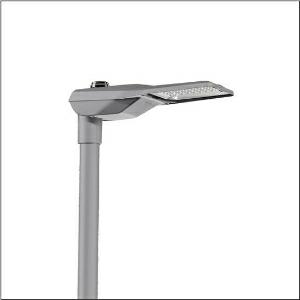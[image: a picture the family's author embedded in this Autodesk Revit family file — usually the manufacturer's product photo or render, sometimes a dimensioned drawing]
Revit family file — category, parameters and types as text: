
# Revit family: streetlight_sl_21_mini___st0_5a_5xe6b37n08gb_187f
name_source: partatom
category: Lighting Fixtures
units: mm (PartAtom-declared; Revit-internal decimal feet)

## family parameters
Cut with Voids When Loaded = No
Host = Face
Light Source = No
Part Type = Normal
Room Calculation Point = No
Round Connector Dimension = Use Diameter
Shared = No

## types (1)
- --- (1 x LED, 5940 lm, 40.4 W, 3000K)
    Apparent Load = 40 VA
    CIE Flux Codes = 41 75 97 100 100
    Color Rendering = 70
    Color Temperature = 3000K
    Default Elevation = 1800 mm
    Description = Streetlight SL 21 mini, mast luminaire, primary light control with lens, of PMMA, primary optical cover: cover, of toughened safety glass, transparent, light distribution: ST0.5a, light emission: direct distribution, primary light characteristic: asymmetric, installation type: side-entry, LED, 3G 1.5mm², High Power LED, rated luminous flux: 5.940lm, luminous efficacy: 147lm/W, light colour: 730, colour temperature: 3000K, control gear: NEMA (7pin), control: overheat protection, pre-setting: linear dimming characteristic, constant luminous flux control, time-dependent luminous flux control, flexible luminous flux parameterisation, mains connection: 230..240V, AC, 50/60Hz, connection cable pre-assembled, cable length: 8,5m, wiring characteristics: H07RN-F, start of lifetime: 40W, end of service life: 41W, reduction: 19W, luminaire housing, of diecast aluminium (EN AC-44300), powder-coated, Siteco® metallic grey (DB 702S), corrosivity category C5 mid according to DIN EN ISO 12944, multi-level sealing system, sealing non-destructively replaceable, inclination adjustable: 0°, 5°, 10°, 15°, length: 628mm, width: 235mm, height: 110mm, spigot size: 42mm (side-entry), mounting height: 4..8m, protection rating (complete): IP66, insulation class (complete): insulation class I (protective earthing), certification: CE, ENEC, ENEC+, VDE, impact resistance: IK10, permissible operating ambient temperature for outdoor applications: -40..+50°C, standard-compliant lighting for roads and squares, packaging unit: 1 piece

Light Distribution: ST0.5a
    Height = 110 mm
    Lamp = 1 x LED
    Lamp Light Flux = 5940 lm
    Lamp Power = 40.4 W
    Lamp count = 1
    Length = 625 mm
    Luminous efficacy = 147 lm/W
    Manufacturer = Siteco
    ModVariant = No
    Model = 5XE6B37N08GB
    Number of Poles = 1
    OnlyDefault = Yes
    Power Factor = 1
    Product Name = Streetlight SL 21 mini | ST0.5a
    Product group = mast luminaire | pylon top
    ProductGroupID = 6100
    Protection Class = Protection class I
    Protection Degree = IP 66
    RLX_Detail_Level = 1
    RLX_Emergency_Light_Flux = 0 lm
    RLX_Emergency_Type = 0
    RLX_Emergency_Type_DB = No
    RlxData = <blob elided: 36873 chars, md5=a9ae22cd>
    Socket = socket
    Standby Power = 0 W
    System Light Flux = 5940 lm
    System Power = 40 W
    Type Comments = factory setting: luminous flux: 100 % | dim-lin: 254 | 812 mA
    Type Image = l_1294379.jpg
    URL = http://relux.com
    VarID = @adj_137536
    Voltage = 0 V
    Weight = 0.00 kg
    Width = 234 mm

## geometry (parser evidence)
native form markers: Blend x4, Sweep x10
no freeform markers — native parametric forms only
